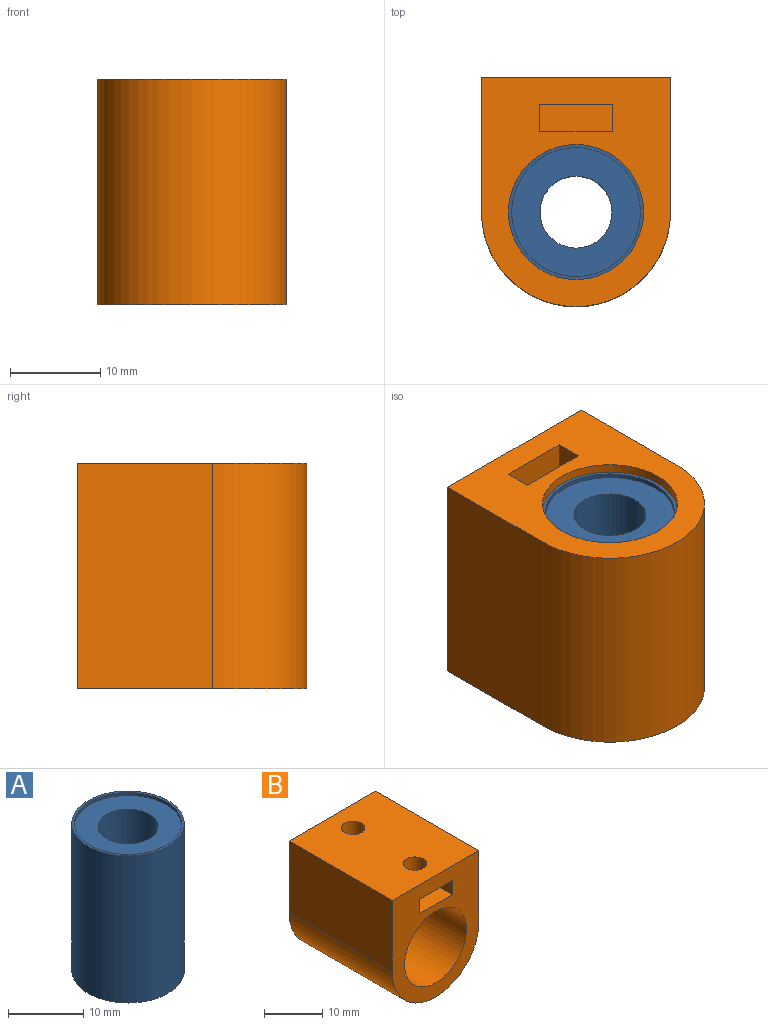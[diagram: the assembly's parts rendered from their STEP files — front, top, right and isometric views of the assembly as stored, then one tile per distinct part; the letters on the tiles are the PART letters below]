
ASSEMBLY  parts=2 mates=1
PART A: 8 faces, bbox 15x15x24 mm
  f0: cylinder r=4mm len=23mm, axis (0,0,-1), area 578.1mm2, adj f5,f7
  f1: plane 15x15mm, normal (0,0,-1), area 16.1mm2, adj f2,f6
  f2: cylinder r=7.5mm len=24mm, axis (0,0,-1), area 1131mm2, adj f1,f3
  f3: plane 15x15mm, normal (0,0,1), area 16.1mm2, adj f2,f4
  f4: cylinder r=7.15mm len=14.3mm, axis (0,0,1), area 22.5mm2, adj f3,f5
  f5: plane 14.3x14.3mm, normal (0,0,1), area 110.3mm2, adj f0,f4
  f6: cylinder r=7.15mm len=14.3mm, axis (0,0,-1), area 22.5mm2, adj f1,f7
  f7: plane 14.3x14.3mm, normal (0,0,-1), area 110.3mm2, adj f0,f6
PART B: 19 faces, bbox 21x25x25.5 mm
  f0: plane 25.5x21mm, normal (0,1,0), area 287.5mm2, adj f2,f3,f4,f5,f6,f14,f15,f16
  f1: cylinder r=2mm len=4mm, axis (0,0,1), area 37.7mm2, adj f5,f9
  f2: plane 25x15mm, normal (-1,0,0), area 375mm2, adj f0,f3,f5,f7
  f3: cylinder r=10.5mm len=25mm, axis (0,1,0), area 824.7mm2, adj f0,f2,f4,f7
  f4: plane 25x15mm, normal (1,0,0), area 375mm2, adj f0,f3,f5,f7
  f5: plane 25x21mm, normal (0,0,1), area 499.9mm2, adj f0,f1,f2,f4,f7,f8
  f6: cylinder r=7.5mm len=25mm, axis (0,1,0), area 1178.1mm2, adj f0,f7
  f7: plane 25.5x21mm, normal (0,-1,0), area 287.5mm2, adj f2,f3,f4,f5,f6,f9,f10,f11
  f8: cylinder r=2mm len=4mm, axis (0,0,1), area 37.7mm2, adj f5,f14
  f9: plane 8x8mm, normal (0,0,-1), area 51.4mm2, adj f1,f7,f10,f11,f12
  f10: plane 8x3mm, normal (1,0,0), area 24mm2, adj f7,f9,f12,f13
  f11: plane 8x3mm, normal (-1,0,0), area 24mm2, adj f7,f9,f12,f13
  f12: plane 8x3mm, normal (0,-1,0), area 24mm2, adj f9,f10,f11,f13
  f13: plane 8x8mm, normal (0,0,1), area 64mm2, adj f7,f10,f11,f12
  f14: plane 8x8mm, normal (0,0,-1), area 51.4mm2, adj f0,f8,f15,f16,f17
  f15: plane 8x3mm, normal (1,0,0), area 24mm2, adj f0,f14,f17,f18
  f16: plane 8x3mm, normal (-1,0,0), area 24mm2, adj f0,f14,f17,f18
  f17: plane 8x3mm, normal (0,1,0), area 24mm2, adj f14,f15,f16,f18
  f18: plane 8x8mm, normal (0,0,1), area 64mm2, adj f0,f15,f16,f17
PLACE A t=(5.79,-3.27,-9.92)mm
PLACE B rot(axis=(-1,0,0),90deg) t=(5.79,-3.27,-21.92)mm
MATE fastened B.f3 <-> A.f0  axis (0,0,1) through (5.79,-3.27,3.08)mm
